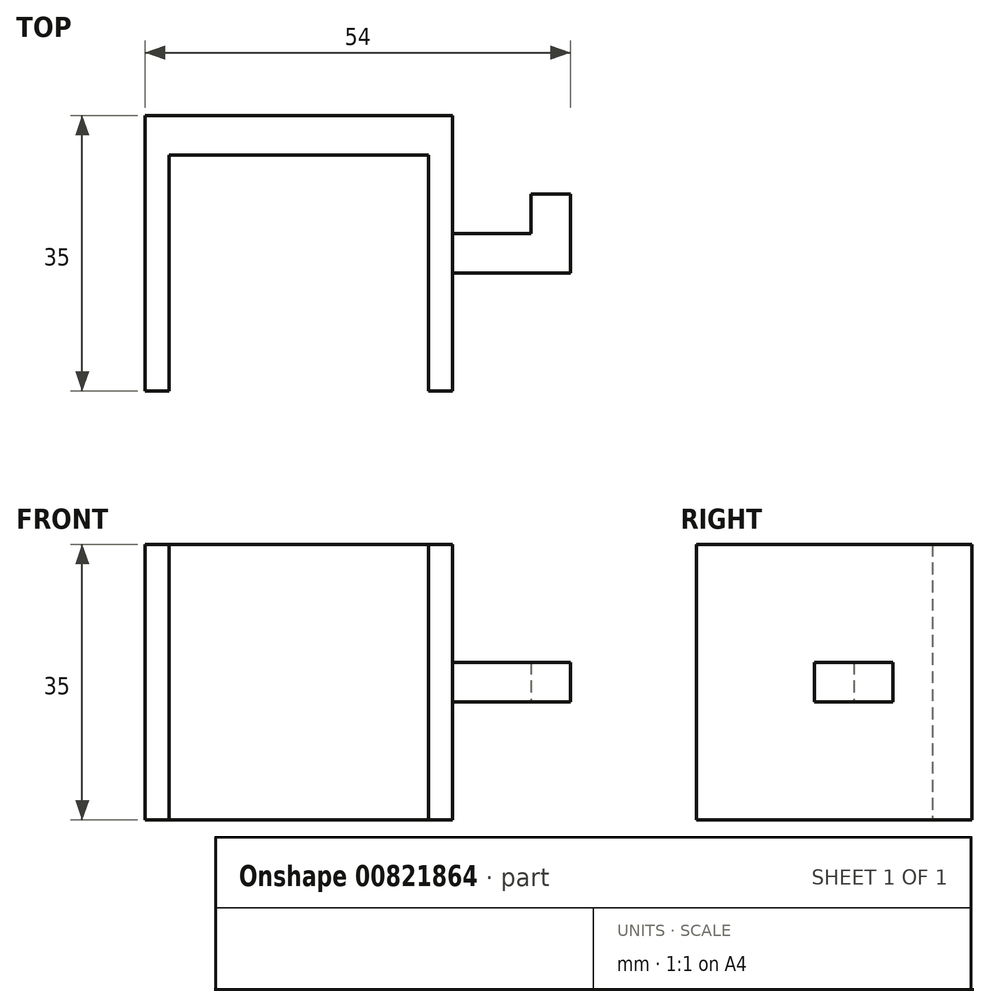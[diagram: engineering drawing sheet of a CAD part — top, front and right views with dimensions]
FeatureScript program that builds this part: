
annotation { "Feature Type Name" : "Feature", "Feature Type Description" : "" }
export const myFeature = defineFeature(function(context is Context, id is Id, definition is map)
    precondition{}
    {
        {
            var Q0;
            Q0=qCreatedBy(makeId("Front.planeOp"),FACE);
            var sketch = newSketch(context, id + "F0", { "sketchPlane" : qUnion([Q0])});
            skLineSegment(sketch, "E0.bottom", {"start": v(-72.03, 45.82) * mm, "end": v(-33.03, 45.82) * mm});
            skLineSegment(sketch, "E0.top", {"start": v(-72.03, 10.82) * mm, "end": v(-33.03, 10.82) * mm});
            skLineSegment(sketch, "E0.left", {"start": v(-72.03, 45.82) * mm, "end": v(-72.03, 10.82) * mm});
            skLineSegment(sketch, "E0.right", {"start": v(-33.03, 45.82) * mm, "end": v(-33.03, 10.82) * mm});
            skSolve(sketch);
        }
        {
            var Q0;
            Q0=makeQuery(id+"F0.imprint","IMPRINT",FACE,{"disambiguationData":[TD([[makeQuery(id+"F0.imprint","IMPRINT",EDGE,{"derivedFrom":sQuery(id+"F0.wireOp",EDGE,"E0.bottom")}),-1.0]])]});
            extrude(context, id + "F1", {"entities" : qUnion([Q0]), "depth" : 35 * mm, "offsetDistance" : 25 * mm});
        }
        {
            var Q0;
            Q0=makeQuery(id+"F1.opExtrude","CAP_FACE",FACE,{"disambiguationData":[OSD([sQuery(id+"F0.wireOp",EDGE,"E0.bottom"),sQuery(id+"F0.wireOp",EDGE,"E0.top"),sQuery(id+"F0.wireOp",EDGE,"E0.left"),sQuery(id+"F0.wireOp",EDGE,"E0.right")])],"isStart":false});
            var sketch = newSketch(context, id + "F2", { "sketchPlane" : qUnion([Q0])});
            skLineSegment(sketch, "E1.bottom", {"start": v(-69.03, 45.82) * mm, "end": v(-36.03, 45.82) * mm});
            skLineSegment(sketch, "E1.top", {"start": v(-69.03, 10.82) * mm, "end": v(-36.03, 10.82) * mm});
            skLineSegment(sketch, "E1.left", {"start": v(-69.03, 45.82) * mm, "end": v(-69.03, 10.82) * mm});
            skLineSegment(sketch, "E1.right", {"start": v(-36.03, 45.82) * mm, "end": v(-36.03, 10.82) * mm});
            skSolve(sketch);
        }
        {
            var Q0;
            Q0=makeQuery(id+"F2.imprint","IMPRINT",FACE,{"disambiguationData":[TD([[makeQuery(id+"F2.imprint","IMPRINT",EDGE,{"derivedFrom":sQuery(id+"F2.wireOp",EDGE,"E1.bottom")}),-1.0]])]});
            extrude(context, id + "F3", {"entities" : qUnion([Q0]), "operationType" : NewBodyOperationType.REMOVE, "oppositeDirection" : true, "depth" : 30 * mm, "offsetDistance" : 25 * mm});
        }
        {
            var Q0;
            Q0=makeQuery(id+"F1.opExtrude","SWEPT_FACE",FACE,{"disambiguationData":[OSD([sQuery(id+"F0.wireOp",EDGE,"E0.right")])]});
            var sketch = newSketch(context, id + "F4", { "sketchPlane" : qUnion([Q0])});
            skLineSegment(sketch, "E2.bottom", {"start": v(-15, 30.82) * mm, "end": v(-20, 30.82) * mm});
            skLineSegment(sketch, "E2.top", {"start": v(-15, 25.82) * mm, "end": v(-20, 25.82) * mm});
            skLineSegment(sketch, "E2.left", {"start": v(-15, 30.82) * mm, "end": v(-15, 25.82) * mm});
            skLineSegment(sketch, "E2.right", {"start": v(-20, 30.82) * mm, "end": v(-20, 25.82) * mm});
            skSolve(sketch);
        }
        {
            var Q0;
            Q0=makeQuery(id+"F4.imprint","IMPRINT",FACE,{"disambiguationData":[TD([[makeQuery(id+"F4.imprint","IMPRINT",EDGE,{"derivedFrom":sQuery(id+"F4.wireOp",EDGE,"E2.bottom")}),1.0]])]});
            extrude(context, id + "F5", {"entities" : qUnion([Q0]), "operationType" : NewBodyOperationType.ADD, "depth" : 15 * mm, "offsetDistance" : 25 * mm});
        }
        {
            var Q0;
            Q0=makeQuery(id+"F5.opExtrude","CAP_FACE",FACE,{"disambiguationData":[OSD([sQuery(id+"F4.wireOp",EDGE,"E2.bottom"),sQuery(id+"F4.wireOp",EDGE,"E2.top"),sQuery(id+"F4.wireOp",EDGE,"E2.left"),sQuery(id+"F4.wireOp",EDGE,"E2.right")])],"isStart":false});
            var sketch = newSketch(context, id + "F6", { "sketchPlane" : qUnion([Q0])});
            skLineSegment(sketch, "E3.bottom", {"start": v(-15, 30.82) * mm, "end": v(-10, 30.82) * mm});
            skLineSegment(sketch, "E3.top", {"start": v(-15, 25.82) * mm, "end": v(-10, 25.82) * mm});
            skLineSegment(sketch, "E3.left", {"start": v(-15, 30.82) * mm, "end": v(-15, 25.82) * mm});
            skLineSegment(sketch, "E3.right", {"start": v(-10, 30.82) * mm, "end": v(-10, 25.82) * mm});
            skSolve(sketch);
        }
        {
            var Q0;
            Q0=makeQuery(id+"F6.imprint","IMPRINT",FACE,{"disambiguationData":[TD([[makeQuery(id+"F6.imprint","IMPRINT",EDGE,{"derivedFrom":sQuery(id+"F6.wireOp",EDGE,"E3.bottom")}),-1.0]])]});
            extrude(context, id + "F7", {"entities" : qUnion([Q0]), "operationType" : NewBodyOperationType.ADD, "oppositeDirection" : true, "depth" : 5 * mm, "offsetDistance" : 25 * mm});
        }
    });
